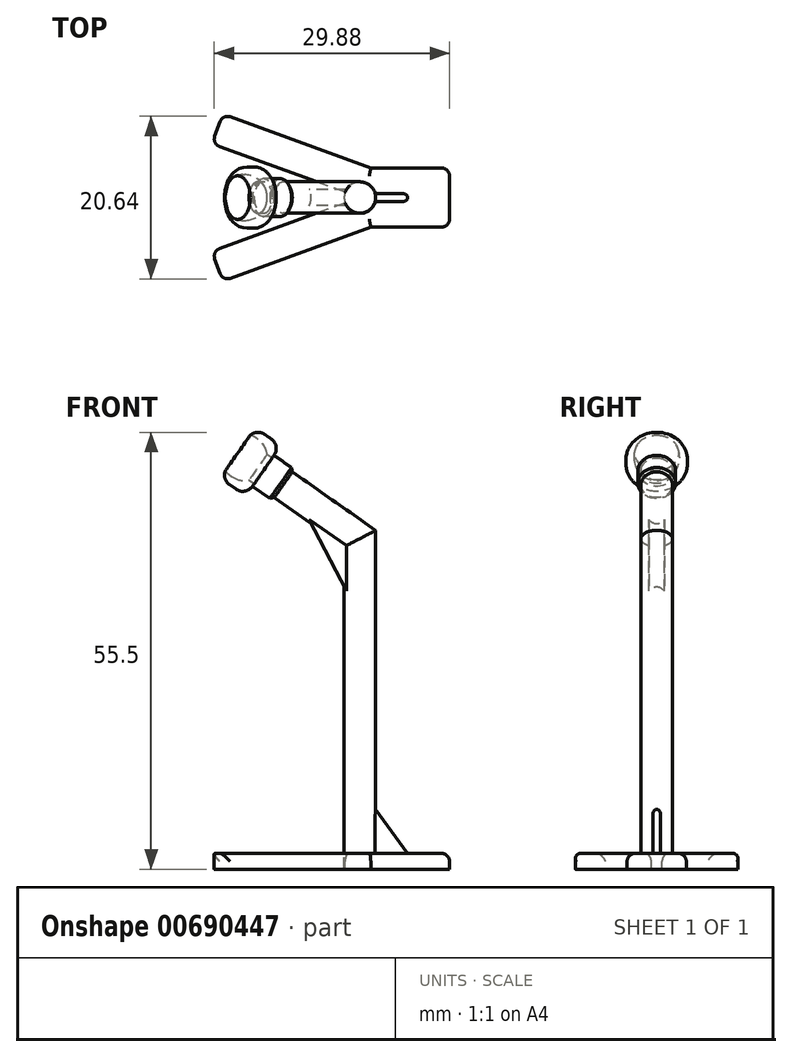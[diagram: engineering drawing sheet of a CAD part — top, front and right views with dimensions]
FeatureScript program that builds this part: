
annotation { "Feature Type Name" : "Feature", "Feature Type Description" : "" }
export const myFeature = defineFeature(function(context is Context, id is Id, definition is map)
    precondition{}
    {
        {
            var Q0;
            Q0=qCreatedBy(makeId("Front.planeOp"),FACE);
            var sketch = newSketch(context, id + "F0", { "sketchPlane" : qUnion([Q0])});
            skLineSegment(sketch, "E0", {"start": v(0, 0) * mm, "end": v(0, 40) * mm});
            skLineSegment(sketch, "E1", {"start": v(0, 40) * mm, "end": v(-12.29, 48.6) * mm});
            skLineSegment(sketch, "E2", {"start": v(0, 40) * mm, "end": v(0, 30) * mm});
            skLineSegment(sketch, "E3", {"start": v(0, 40) * mm, "end": v(-8.2, 45.74) * mm});
            skLineSegment(sketch, "E4", {"start": v(-8.2, 45.74) * mm, "end": v(0, 30) * mm});
            skSolve(sketch);
        }
        {
            var Q0;
            Q0=qCreatedBy(makeId("Top.planeOp"),FACE);
            var sketch = newSketch(context, id + "F1", { "sketchPlane" : qUnion([Q0])});
            skCircle(sketch, "E5", {"center": v(0, 0) * mm, "radius": 2 * mm});
            skSolve(sketch);
        }
        {
            var Q0;
            Q0=makeQuery(id+"F1.imprint","IMPRINT",FACE,{"disambiguationData":[TD([[makeQuery(id+"F1.imprint","IMPRINT",EDGE,{"derivedFrom":sQuery(id+"F1.wireOp",EDGE,"E5")}),1.0]])]});
            var Q1;
            Q1=sQuery(id+"F0.wireOp",EDGE,"E0");
            var Q2;
            Q2=sQuery(id+"F0.wireOp",EDGE,"E1");
            sweep(context, id + "F2", {"profiles" : qUnion([Q0]), "path" : qUnion([Q1, Q2])});
        }
        {
            var Q0;
            Q0 = qSketchRegion(id + "F0", true);
            extrude(context, id + "F3", {"entities" : qUnion([Q0]), "operationType" : NewBodyOperationType.ADD, "endBound" : BoundingType.SYMMETRIC, "depth" : 2 * mm, "offsetDistance" : 25 * mm});
        }
        {
            var Q0;
            Q0=makeQuery(id+"F2.opSweep","CAP_FACE",FACE,{"disambiguationData":[OSD([sQuery(id+"F0.wireOp",VERTEX,"E1.end"),sQuery(id+"F1.wireOp",EDGE,"E5")])],"isStart":false});
            var sketch = newSketch(context, id + "F4", { "sketchPlane" : qUnion([Q0])});
            skCircle(sketch, "E6", {"center": v(0, 32.77) * mm, "radius": 2.9 * mm});
            skCircle(sketch, "E7", {"center": v(0, 32.77) * mm, "radius": 3.9 * mm});
            skSolve(sketch);
        }
        {
            var Q0;
            Q0=makeQuery(id+"F4.imprint","IMPRINT",FACE,{"disambiguationData":[TD([[makeQuery(id+"F4.imprint","IMPRINT",EDGE,{"derivedFrom":sQuery(id+"F4.wireOp",EDGE,"E6")}),-1.0]])]});
            var Q1;
            Q1=makeQuery(id+"F4.imprint","IMPRINT",FACE,{"disambiguationData":[TD([[makeQuery(id+"F4.imprint","IMPRINT",EDGE,{"derivedFrom":sQuery(id+"F4.wireOp",EDGE,"E6")}),1.0]])]});
            extrude(context, id + "F5", {"entities" : qUnion([Q0, Q1]), "operationType" : NewBodyOperationType.ADD, "depth" : 4 * mm, "offsetDistance" : 25 * mm});
        }
        {
            var Q0;
            Q0=makeQuery(id+"F5.opExtrude","CAP_EDGE",EDGE,{"disambiguationData":[OSD([sQuery(id+"F4.wireOp",EDGE,"E7")])],"isStart":false});
            var Q1;
            Q1=makeQuery(id+"F5.opExtrude","CAP_EDGE",EDGE,{"disambiguationData":[OSD([sQuery(id+"F4.wireOp",EDGE,"E7")])],"isStart":true});
            fillet(context, id + "F6", {"entities" : qUnion([Q0, Q1]), "radius" : 1.5 * mm, "tangentPropagation" : true, "allowEdgeOverflow" : false});
        }
        {
            var Q0;
            Q0=makeQuery(id+"F2.opSweep","CAP_FACE",FACE,{"disambiguationData":[OSD([sQuery(id+"F0.wireOp",VERTEX,"E1.end"),sQuery(id+"F1.wireOp",EDGE,"E5")])],"isStart":false});
            var sketch = newSketch(context, id + "F7", { "sketchPlane" : qUnion([Q0])});
            skCircle(sketch, "E8", {"center": v(0, 32.77) * mm, "radius": 2.9 * mm});
            skSolve(sketch);
        }
        {
            var Q0;
            Q0 = qSketchRegion(id + "F7", true);
            extrude(context, id + "F8", {"entities" : qUnion([Q0]), "depth" : 6 * mm, "offsetDistance" : 25 * mm});
        }
        {
            var Q0;
            Q0=makeQuery(id+"F8.opExtrude","CAP_EDGE",EDGE,{"disambiguationData":[OSD([sQuery(id+"F7.wireOp",EDGE,"E8")])],"isStart":false});
            var Q1;
            Q1=makeQuery(id+"F8.opExtrude","CAP_EDGE",EDGE,{"disambiguationData":[OSD([sQuery(id+"F7.wireOp",EDGE,"E8")])],"isStart":true});
            fillet(context, id + "F9", {"entities" : qUnion([Q0, Q1]), "radius" : 2.9 * mm, "tangentPropagation" : true, "allowEdgeOverflow" : false});
        }
        {
            var Q0;
            Q0=makeQuery(id+"F8.opExtrude","SWEPT_BODY",BODY,{"disambiguationData":[OSD([sQuery(id+"F7.wireOp",EDGE,"E8")])]});
            var Q1;
            Q1=makeQuery(id+"F5.opExtrude","SWEPT_BODY",BODY,{"disambiguationData":[OSD([sQuery(id+"F0.wireOp",VERTEX,"E1.end"),sQuery(id+"F1.wireOp",EDGE,"E5"),sQuery(id+"F4.wireOp",EDGE,"E7")])]});
            booleanBodies(context, id + "F10", {"operationType" : BooleanOperationType.SUBTRACTION, "tools" : qUnion([Q0]), "targets" : qUnion([Q1])});
        }
        {
            var Q0;
            Q0=makeQuery(id+"F5.opExtrude","CAP_FACE",FACE,{"disambiguationData":[OSD([sQuery(id+"F0.wireOp",VERTEX,"E1.end"),sQuery(id+"F1.wireOp",EDGE,"E5"),sQuery(id+"F4.wireOp",EDGE,"E7")])],"isStart":true});
            var Q1;
            Q1=makeQuery(id+"F2.opSweep","CAP_FACE",FACE,{"disambiguationData":[OSD([sQuery(id+"F0.wireOp",VERTEX,"E1.end"),sQuery(id+"F1.wireOp",EDGE,"E5")])],"isStart":false});
            extrude(context, id + "F11", {"entities" : qUnion([Q0, Q1]), "operationType" : NewBodyOperationType.ADD, "depth" : 5 * mm, "offsetDistance" : 25 * mm});
        }
        {
            var Q0;
            Q0=makeQuery(id+"F11.opExtrude","CAP_EDGE",EDGE,{"disambiguationData":[OSD([sQuery(id+"F0.wireOp",VERTEX,"E1.end"),sQuery(id+"F1.wireOp",EDGE,"E5"),sQuery(id+"F4.wireOp",EDGE,"E7")])],"isStart":false});
            chamfer(context, id + "F12", {"entities" : qUnion([Q0]), "width" : 2.3 * mm, "tangentPropagation" : true});
        }
        {
            var Q0;
            Q0=makeQuery(id+"F2.opSweep","CAP_FACE",FACE,{"disambiguationData":[OSD([sQuery(id+"F0.wireOp",VERTEX,"E0.start"),sQuery(id+"F1.wireOp",EDGE,"E5")])],"isStart":true});
            var sketch = newSketch(context, id + "F13", { "sketchPlane" : qUnion([Q0])});
            skLineSegment(sketch, "E9.bottom", {"start": v(0, 0) * mm, "end": v(-18.8, 6.84) * mm});
            skLineSegment(sketch, "E9.top", {"start": v(1.37, 3.76) * mm, "end": v(-17.43, 10.6) * mm});
            skLineSegment(sketch, "E9.right", {"start": v(-18.8, 6.84) * mm, "end": v(-17.43, 10.6) * mm});
            skLineSegment(sketch, "E10.MirrorCS", {"start": v(0, 0) * mm, "end": v(-18.8, -6.84) * mm});
            skLineSegment(sketch, "E11.MirrorCS", {"start": v(1.37, -3.76) * mm, "end": v(-17.43, -10.6) * mm});
            skLineSegment(sketch, "E12.MirrorCS", {"start": v(-18.8, -6.84) * mm, "end": v(-17.43, -10.6) * mm});
            skLineSegment(sketch, "E13.bottom", {"start": v(1.37, 3.76) * mm, "end": v(11.37, 3.76) * mm});
            skLineSegment(sketch, "E13.top", {"start": v(1.37, -3.76) * mm, "end": v(11.37, -3.76) * mm});
            skLineSegment(sketch, "E13.right", {"start": v(11.37, 3.76) * mm, "end": v(11.37, -3.76) * mm});
            skSolve(sketch);
        }
        {
            var Q0;
            Q0=makeQuery(id+"F13.imprint","IMPRINT",FACE,{"disambiguationData":[TD([[makeQuery(id+"F13.imprint","IMPRINT",EDGE,{"derivedFrom":sQuery(id+"F13.wireOp",EDGE,"E9.top")}),1.0]])]});
            var Q1;
            {var subQ0=sQuery(id+"F13.wireOp",EDGE,"E10.MirrorCS");var subQ1=sQuery(id+"F13.wireOp",EDGE,"E9.bottom");var subQ2=makeQuery(id+"F13.imprint","INTERSECT",VERTEX,{"derivedFrom":[subQ1,subQ0]});Q1=makeQuery(id+"F13.imprint","IMPRINT",FACE,{"disambiguationData":[TD([[makeQuery(id+"F13.imprint","IMPRINT",EDGE,{"disambiguationData":[TD([[subQ2,-1.0]])],"derivedFrom":subQ1}),-1.0]])]});}
            var Q2;
            {var subQ0=sQuery(id+"F13.wireOp",EDGE,"E10.MirrorCS");var subQ1=sQuery(id+"F13.wireOp",EDGE,"E9.bottom");var subQ2=makeQuery(id+"F13.imprint","INTERSECT",VERTEX,{"derivedFrom":[subQ1,subQ0]});Q2=makeQuery(id+"F13.imprint","IMPRINT",FACE,{"disambiguationData":[TD([[makeQuery(id+"F13.imprint","IMPRINT",EDGE,{"disambiguationData":[TD([[subQ2,-1.0]])],"derivedFrom":subQ1}),1.0]])]});}
            extrude(context, id + "F14", {"entities" : qUnion([Q0, Q1, Q2]), "operationType" : NewBodyOperationType.ADD, "depth" : 2 * mm, "offsetDistance" : 25 * mm});
        }
        {
            var Q0;
            Q0=qCreatedBy(makeId("Front.planeOp"),FACE);
            var sketch = newSketch(context, id + "F15", { "sketchPlane" : qUnion([Q0])});
            skLineSegment(sketch, "E14", {"start": v(6.05, 0) * mm, "end": v(0, 8.38) * mm});
            skLineSegment(sketch, "E15", {"start": v(0, 8.38) * mm, "end": v(0, 0) * mm});
            skLineSegment(sketch, "E16", {"start": v(0, 0) * mm, "end": v(6.05, 0) * mm});
            skSolve(sketch);
        }
        {
            var Q0;
            Q0=makeQuery(id+"F15.imprint","IMPRINT",FACE,{"disambiguationData":[TD([[makeQuery(id+"F15.imprint","IMPRINT",EDGE,{"derivedFrom":sQuery(id+"F15.wireOp",EDGE,"E14")}),1.0]])]});
            extrude(context, id + "F16", {"entities" : qUnion([Q0]), "operationType" : NewBodyOperationType.ADD, "endBound" : BoundingType.SYMMETRIC, "depth" : 1 * mm, "offsetDistance" : 25 * mm});
        }
        {
            var Q0;
            Q0=makeQuery(id+"F14.opExtrude","SWEPT_EDGE",EDGE,{"disambiguationData":[OSD([sQuery(id+"F13.wireOp",EDGE,"E11.MirrorCS"),sQuery(id+"F13.wireOp",EDGE,"E12.MirrorCS")])]});
            var Q1;
            Q1=makeQuery(id+"F14.opExtrude","SWEPT_EDGE",EDGE,{"disambiguationData":[OSD([sQuery(id+"F13.wireOp",EDGE,"E10.MirrorCS"),sQuery(id+"F13.wireOp",EDGE,"E12.MirrorCS")])]});
            var Q2;
            Q2=makeQuery(id+"F14.opExtrude","CAP_EDGE",EDGE,{"disambiguationData":[OSD([sQuery(id+"F13.wireOp",EDGE,"E11.MirrorCS")])],"isStart":true});
            var Q3;
            Q3=makeQuery(id+"F14.opExtrude","CAP_EDGE",EDGE,{"disambiguationData":[OSD([sQuery(id+"F13.wireOp",EDGE,"E10.MirrorCS")])],"isStart":true});
            var Q4;
            Q4=makeQuery(id+"F14.opExtrude","SWEPT_EDGE",EDGE,{"disambiguationData":[OSD([sQuery(id+"F13.wireOp",EDGE,"E9.bottom"),sQuery(id+"F13.wireOp",EDGE,"E9.right")])]});
            var Q5;
            Q5=makeQuery(id+"F14.opExtrude","CAP_EDGE",EDGE,{"disambiguationData":[OSD([sQuery(id+"F13.wireOp",EDGE,"E9.bottom")])],"isStart":true});
            var Q6;
            Q6=makeQuery(id+"F14.opExtrude","CAP_EDGE",EDGE,{"disambiguationData":[OSD([sQuery(id+"F13.wireOp",EDGE,"E9.top")])],"isStart":true});
            var Q7;
            Q7=makeQuery(id+"F14.opExtrude","SWEPT_EDGE",EDGE,{"disambiguationData":[OSD([sQuery(id+"F13.wireOp",EDGE,"E9.top"),sQuery(id+"F13.wireOp",EDGE,"E9.right")])]});
            var Q8;
            Q8=makeQuery(id+"F14.opExtrude","CAP_EDGE",EDGE,{"disambiguationData":[OSD([sQuery(id+"F13.wireOp",EDGE,"E13.bottom")])],"isStart":true});
            var Q9;
            Q9=makeQuery(id+"F14.opExtrude","CAP_EDGE",EDGE,{"disambiguationData":[OSD([sQuery(id+"F13.wireOp",EDGE,"E13.top")])],"isStart":true});
            var Q10;
            Q10=makeQuery(id+"F14.opExtrude","SWEPT_EDGE",EDGE,{"disambiguationData":[OSD([sQuery(id+"F13.wireOp",EDGE,"E13.bottom"),sQuery(id+"F13.wireOp",EDGE,"E13.right")])]});
            var Q11;
            Q11=makeQuery(id+"F14.opExtrude","SWEPT_EDGE",EDGE,{"disambiguationData":[OSD([sQuery(id+"F13.wireOp",EDGE,"E13.top"),sQuery(id+"F13.wireOp",EDGE,"E13.right")])]});
            var Q12;
            Q12=makeQuery(id+"F14.opExtrude","CAP_EDGE",EDGE,{"disambiguationData":[OSD([sQuery(id+"F13.wireOp",EDGE,"E13.right")])],"isStart":true});
            fillet(context, id + "F17", {"entities" : qUnion([Q0, Q1, Q2, Q3, Q4, Q5, Q6, Q7, Q8, Q9, Q10, Q11, Q12]), "radius" : 1 * mm, "tangentPropagation" : true, "allowEdgeOverflow" : false});
        }
        {
            var Q0;
            Q0=makeQuery(id+"F16.opExtrude","CAP_EDGE",EDGE,{"disambiguationData":[OSD([sQuery(id+"F15.wireOp",EDGE,"E14")])],"isStart":false});
            var Q1;
            Q1=makeQuery(id+"F16.opExtrude","CAP_EDGE",EDGE,{"disambiguationData":[OSD([sQuery(id+"F15.wireOp",EDGE,"E14")])],"isStart":true});
            fillet(context, id + "F18", {"entities" : qUnion([Q0, Q1]), "radius" : 0.5 * mm, "tangentPropagation" : true, "allowEdgeOverflow" : false});
        }
    });
